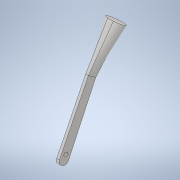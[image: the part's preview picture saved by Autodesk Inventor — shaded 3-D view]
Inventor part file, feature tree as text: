
AUTODESK INVENTOR PART (.ipt)
format: ipt  version: 2020 (Build 240168000, 168)  size: 186,880 bytes
history: native  units: mm
features: thicken_offset x4, sketch x2, extrude x1, fillet x1, plane x1, loft x1, other x1
ambient origin geometry x8: Origin, YZ Plane, XZ Plane, XY Plane, X Axis, Y Axis, Z Axis, Center Point
bodies: Solid1 (feature_tree)
feature tree (11):
  extrude  "Extrusion1"  Depth=50.0mm
  fillet  "Fillet1"  Radius=50.0mm
  thicken_offset  "Thicken1"
  thicken_offset  "Thicken2"
  thicken_offset  "Thicken3"
  plane  "Work Plane1"
  loft  "Loft1"
  thicken_offset  "Thicken4"
  sketch  "Sketch1"  dims[d2=0.0mm d5=50.0mm d7=50.0mm]
  sketch  "Sketch3"  dims[d9=50.0mm d12=0.0mm d13=90.0deg d14=0.0mm d15=90.0deg d17=40.0mm]
  other  "Edges1"
